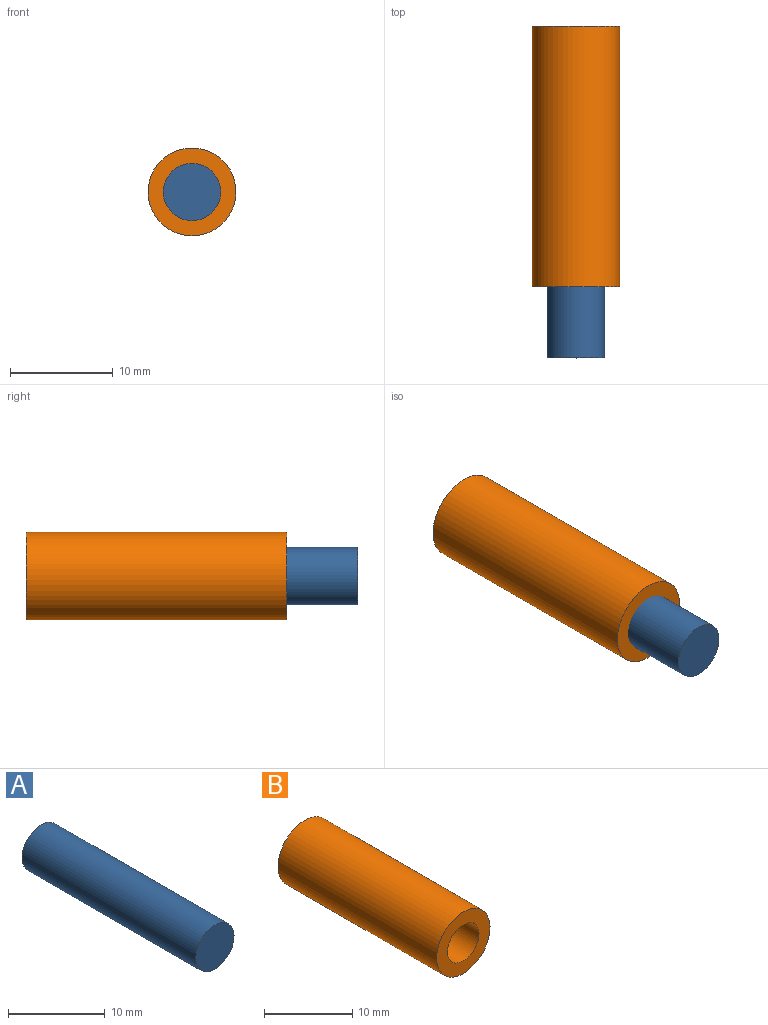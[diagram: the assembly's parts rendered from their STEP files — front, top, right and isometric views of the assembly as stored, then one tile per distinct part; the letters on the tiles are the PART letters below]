
ASSEMBLY  parts=2 mates=2
PART A: 3 faces, bbox 5.6x25.4x5.6 mm
  f0: cylinder r=2.79mm len=25.4mm, axis (0,-1,0), area 445.9mm2, adj f1,f2
  f1: plane 5.59x5.59mm, normal (0,-1,0), area 24.5mm2, adj f0
  f2: plane 5.59x5.59mm, normal (0,1,0), area 24.5mm2, adj f0
PART B: 4 faces, bbox 8.6x25.4x8.6 mm
  f0: cylinder r=2.52mm len=25.4mm, axis (0,-1,0), area 402.1mm2, adj f2,f3
  f1: cylinder r=4.28mm len=25.4mm, axis (0,-1,0), area 683.1mm2, adj f2,f3
  f2: plane 8.56x8.56mm, normal (0,-1,0), area 37.6mm2, adj f0,f1
  f3: plane 8.56x8.56mm, normal (0,1,0), area 37.6mm2, adj f0,f1
PLACE A t=(7.9,35.29,-1.69)mm
PLACE B t=(-32.07,42.24,-18.94)mm
MATE slider A.f0 <-> B.f0  axis (0,-1,0) through (-15.85,22.59,-8.83)mm
MATE slider B.f0 <-> A.f0  axis (0,-1,0) through (-15.85,29.54,-8.83)mm
